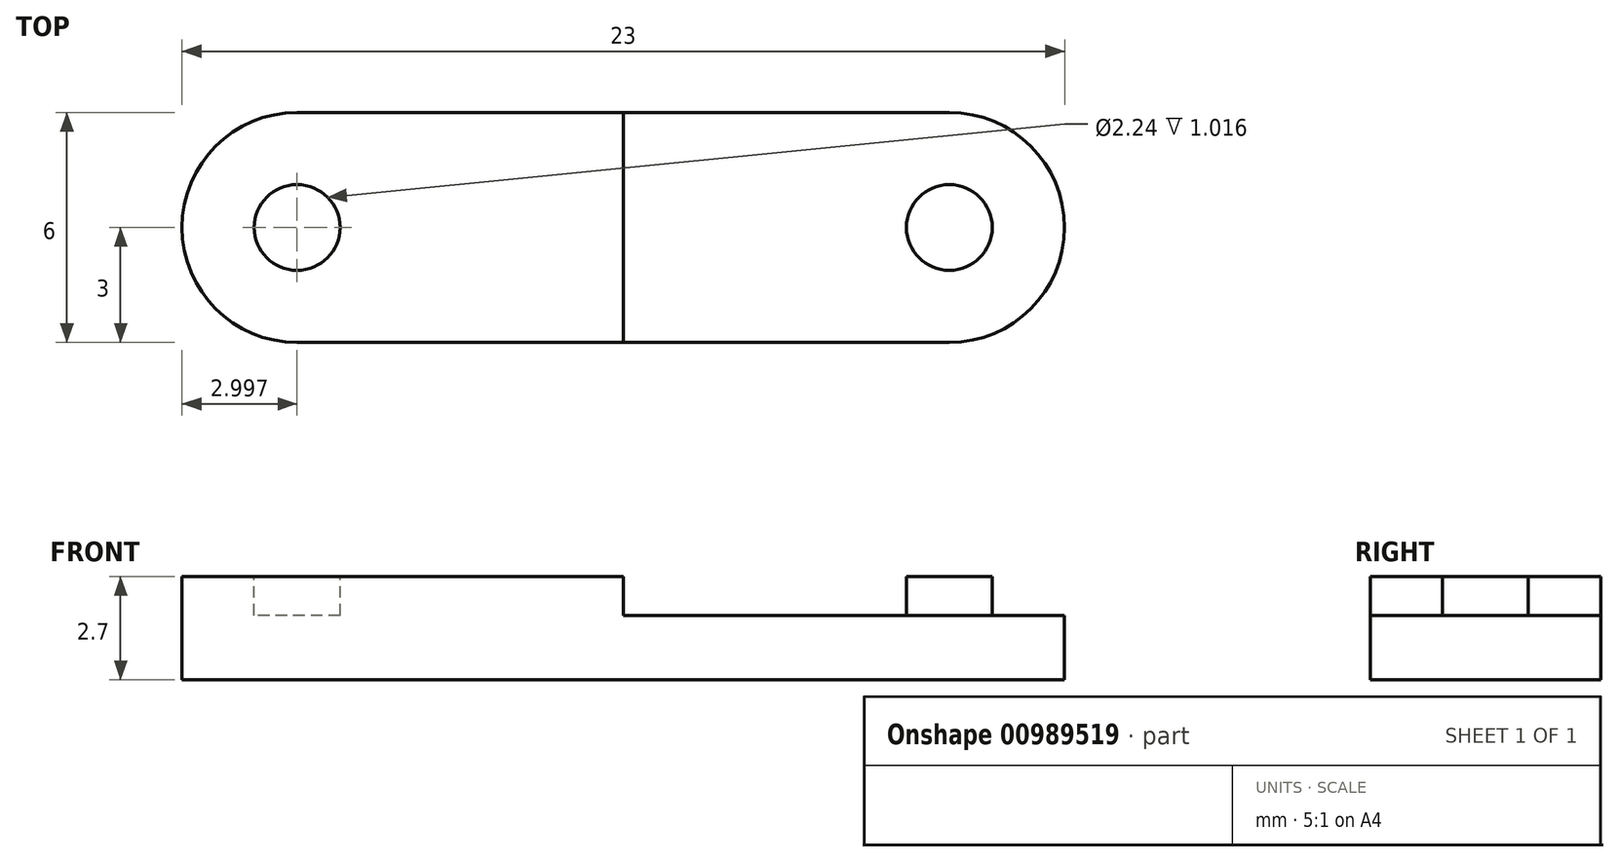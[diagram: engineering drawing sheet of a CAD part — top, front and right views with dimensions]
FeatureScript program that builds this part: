
annotation { "Feature Type Name" : "Feature", "Feature Type Description" : "" }
export const myFeature = defineFeature(function(context is Context, id is Id, definition is map)
    precondition{}
    {
        {
            var Q0;
            Q0=qCreatedBy(makeId("Top.planeOp"),FACE);
            var sketch = newSketch(context, id + "F0", { "sketchPlane" : qUnion([Q0])});
            skArc(sketch, "E0", {"start": v(-12.73, 6) * mm, "mid": v(-15.73, 3) * mm, "end": v(-12.73, 0) * mm});
            skLineSegment(sketch, "E1", {"start": v(-12.73, 6) * mm, "end": v(4.27, 6) * mm});
            skLineSegment(sketch, "E2", {"start": v(4.27, 0) * mm, "end": v(-12.73, 0) * mm});
            skArc(sketch, "E3", {"start": v(4.27, 0) * mm, "mid": v(7.27, 3) * mm, "end": v(4.27, 6) * mm});
            skSolve(sketch);
        }
        {
            var Q0;
            Q0 = qSketchRegion(id + "F0", true);
            extrude(context, id + "F1", {"entities" : qUnion([Q0]), "depth" : 2.7 * mm, "offsetDistance" : 25.4 * mm});
        }
        {
            var Q0;
            Q0=makeQuery(id+"F1.opExtrude","CAP_FACE",FACE,{"disambiguationData":[OSD([sQuery(id+"F0.wireOp",EDGE,"E0"),sQuery(id+"F0.wireOp",EDGE,"E1"),sQuery(id+"F0.wireOp",EDGE,"E2"),sQuery(id+"F0.wireOp",EDGE,"E3")])],"isStart":false});
            var sketch = newSketch(context, id + "F2", { "sketchPlane" : qUnion([Q0])});
            skCircle(sketch, "E4", {"center": v(-12.73, 3) * mm, "radius": 1.12 * mm});
            skLineSegment(sketch, "E5", {"start": v(-4.23, 0) * mm, "end": v(-4.23, 6) * mm});
            skCircle(sketch, "E6.MirrorC", {"center": v(4.27, 3) * mm, "radius": 1.12 * mm});
            skSolve(sketch);
        }
        {
            var Q0;
            Q0=makeQuery(id+"F2.imprint","IMPRINT",FACE,{"disambiguationData":[TD([[makeQuery(id+"F2.imprint","IMPRINT",EDGE,{"derivedFrom":sQuery(id+"F2.wireOp",EDGE,"E6.MirrorC")}),-1.0]])]});
            var Q1;
            Q1=makeQuery(id+"F2.imprint","IMPRINT",FACE,{"disambiguationData":[TD([[makeQuery(id+"F2.imprint","IMPRINT",EDGE,{"derivedFrom":sQuery(id+"F2.wireOp",EDGE,"E4")}),1.0]])]});
            extrude(context, id + "F3", {"entities" : qUnion([Q0, Q1]), "operationType" : NewBodyOperationType.REMOVE, "oppositeDirection" : true, "depth" : 1.02 * mm, "offsetDistance" : 25.4 * mm});
        }
    });
